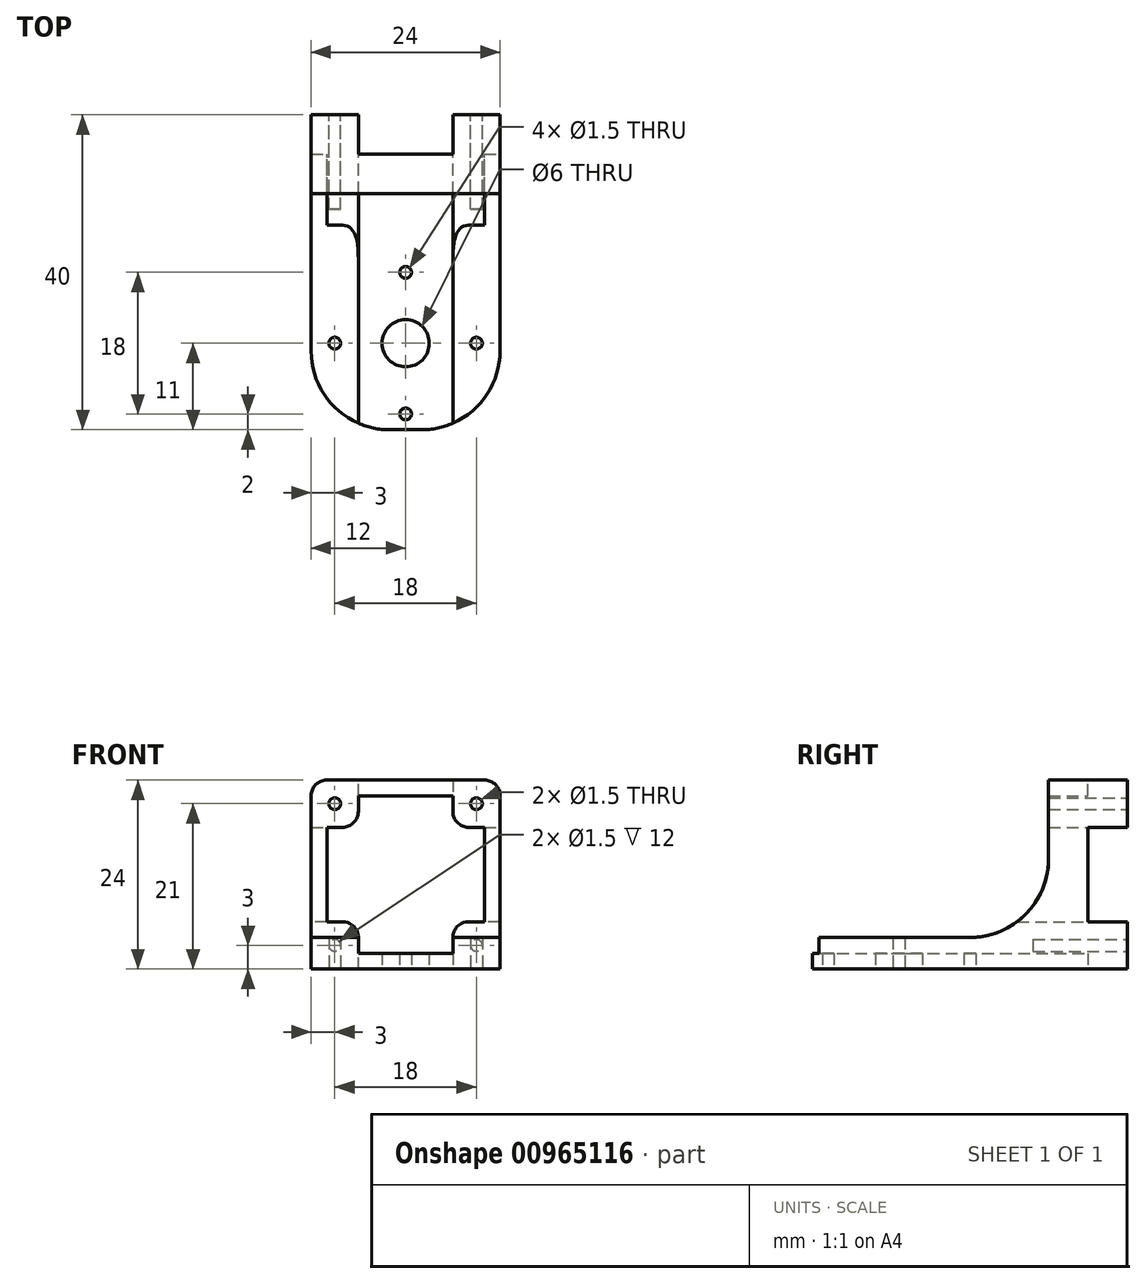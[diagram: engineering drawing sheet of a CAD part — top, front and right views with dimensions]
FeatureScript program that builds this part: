
annotation { "Feature Type Name" : "Feature", "Feature Type Description" : "" }
export const myFeature = defineFeature(function(context is Context, id is Id, definition is map)
    precondition{}
    {
        {
            var Q0;
            Q0=qCreatedBy(makeId("Top.planeOp"),FACE);
            var sketch = newSketch(context, id + "F0", { "sketchPlane" : qUnion([Q0])});
            skLineSegment(sketch, "E0.bottom", {"start": v(0, 0) * mm, "end": v(24, 0) * mm});
            skLineSegment(sketch, "E0.top", {"start": v(0, 35) * mm, "end": v(24, 35) * mm});
            skLineSegment(sketch, "E0.left", {"start": v(0, 0) * mm, "end": v(0, 35) * mm});
            skLineSegment(sketch, "E0.right", {"start": v(24, 0) * mm, "end": v(24, 35) * mm});
            skLineSegment(sketch, "E1", {"start": v(2.83, 11) * mm, "end": v(19.55, 11) * mm, "construction": true});
            skLineSegment(sketch, "E2", {"start": v(12, 2.3) * mm, "end": v(12, 16.8) * mm, "construction": true});
            skLineSegment(sketch, "E3", {"start": v(2, 21) * mm, "end": v(22, 1) * mm, "construction": true});
            skLineSegment(sketch, "E4", {"start": v(22, 21) * mm, "end": v(2, 1) * mm, "construction": true});
            skCircle(sketch, "E5", {"center": v(12, 2) * mm, "radius": 0.75 * mm});
            skCircle(sketch, "E6", {"center": v(3, 11) * mm, "radius": 0.75 * mm});
            skCircle(sketch, "E7", {"center": v(12, 20) * mm, "radius": 0.75 * mm});
            skCircle(sketch, "E8", {"center": v(21, 11) * mm, "radius": 0.75 * mm});
            skCircle(sketch, "E9", {"center": v(12, 11) * mm, "radius": 3 * mm});
            skSolve(sketch);
        }
        {
            var Q0;
            Q0=makeQuery(id+"F0.imprint","IMPRINT",FACE,{"disambiguationData":[TD([[makeQuery(id+"F0.imprint","IMPRINT",EDGE,{"derivedFrom":sQuery(id+"F0.wireOp",EDGE,"E0.bottom")}),1.0]])]});
            extrude(context, id + "F1", {"entities" : qUnion([Q0]), "depth" : 24 * mm, "offsetDistance" : 25 * mm});
        }
        {
            var Q0;
            Q0=makeQuery(id+"F1.opExtrude","SWEPT_FACE",FACE,{"disambiguationData":[OSD([sQuery(id+"F0.wireOp",EDGE,"E0.top")])]});
            var sketch = newSketch(context, id + "F2", { "sketchPlane" : qUnion([Q0])});
            skCircle(sketch, "E10", {"center": v(-3, 3) * mm, "radius": 0.75 * mm});
            skCircle(sketch, "E11", {"center": v(-21, 3) * mm, "radius": 0.75 * mm});
            skCircle(sketch, "E12", {"center": v(-21, 21) * mm, "radius": 0.75 * mm});
            skCircle(sketch, "E13", {"center": v(-3, 21) * mm, "radius": 0.75 * mm});
            skLineSegment(sketch, "E14", {"start": v(-6, 22) * mm, "end": v(-18, 22) * mm});
            skLineSegment(sketch, "E15", {"start": v(-22, 18) * mm, "end": v(-22, 6) * mm});
            skLineSegment(sketch, "E16", {"start": v(-18, 2) * mm, "end": v(-6, 2) * mm});
            skLineSegment(sketch, "E17", {"start": v(-2, 18) * mm, "end": v(-2, 6) * mm});
            skLineSegment(sketch, "E18", {"start": v(-18, 22) * mm, "end": v(-18, 18) * mm});
            skLineSegment(sketch, "E19", {"start": v(-18, 18) * mm, "end": v(-22, 18) * mm});
            skLineSegment(sketch, "E20", {"start": v(-22, 6) * mm, "end": v(-18, 6) * mm});
            skLineSegment(sketch, "E21", {"start": v(-18, 6) * mm, "end": v(-18, 2) * mm});
            skLineSegment(sketch, "E22", {"start": v(-6, 2) * mm, "end": v(-6, 6) * mm});
            skLineSegment(sketch, "E23", {"start": v(-6, 6) * mm, "end": v(-2, 6) * mm});
            skLineSegment(sketch, "E24", {"start": v(-2, 18) * mm, "end": v(-6, 18) * mm});
            skLineSegment(sketch, "E25", {"start": v(-6, 18) * mm, "end": v(-6, 22) * mm});
            skLineSegment(sketch, "E26.bottom", {"start": v(-18, 22) * mm, "end": v(-6, 22) * mm});
            skLineSegment(sketch, "E26.top", {"start": v(-18, 24) * mm, "end": v(-6, 24) * mm});
            skLineSegment(sketch, "E26.left", {"start": v(-18, 22) * mm, "end": v(-18, 24) * mm});
            skLineSegment(sketch, "E26.right", {"start": v(-6, 22) * mm, "end": v(-6, 24) * mm});
            skLineSegment(sketch, "E27.bottom", {"start": v(-2, 18) * mm, "end": v(0, 18) * mm});
            skLineSegment(sketch, "E27.top", {"start": v(-2, 6) * mm, "end": v(0, 6) * mm});
            skLineSegment(sketch, "E27.right", {"start": v(0, 18) * mm, "end": v(0, 6) * mm});
            skLineSegment(sketch, "E28.bottom", {"start": v(-22, 18) * mm, "end": v(-24, 18) * mm});
            skLineSegment(sketch, "E28.top", {"start": v(-22, 6) * mm, "end": v(-24, 6) * mm});
            skLineSegment(sketch, "E28.right", {"start": v(-24, 18) * mm, "end": v(-24, 6) * mm});
            skLineSegment(sketch, "E29.top", {"start": v(-18, 0) * mm, "end": v(-6, 0) * mm});
            skLineSegment(sketch, "E29.left", {"start": v(-18, 2) * mm, "end": v(-18, 0) * mm});
            skLineSegment(sketch, "E29.right", {"start": v(-6, 2) * mm, "end": v(-6, 0) * mm});
            skSolve(sketch);
        }
        {
            var Q0;
            Q0=makeQuery(id+"F2.imprint","IMPRINT",FACE,{"disambiguationData":[TD([[makeQuery(id+"F2.imprint","IMPRINT",EDGE,{"derivedFrom":sQuery(id+"F2.wireOp",EDGE,"E12")}),1.0]])]});
            var Q1;
            Q1=makeQuery(id+"F2.imprint","IMPRINT",FACE,{"disambiguationData":[TD([[makeQuery(id+"F2.imprint","IMPRINT",EDGE,{"derivedFrom":sQuery(id+"F2.wireOp",EDGE,"E13")}),1.0]])]});
            var Q2;
            Q2=makeQuery(id+"F2.imprint","IMPRINT",FACE,{"disambiguationData":[TD([[makeQuery(id+"F2.imprint","IMPRINT",EDGE,{"derivedFrom":sQuery(id+"F2.wireOp",EDGE,"E10")}),1.0]])]});
            var Q3;
            Q3=makeQuery(id+"F2.imprint","IMPRINT",FACE,{"disambiguationData":[TD([[makeQuery(id+"F2.imprint","IMPRINT",EDGE,{"derivedFrom":sQuery(id+"F2.wireOp",EDGE,"E11")}),1.0]])]});
            extrude(context, id + "F3", {"entities" : qUnion([Q0, Q1, Q2, Q3]), "operationType" : NewBodyOperationType.REMOVE, "oppositeDirection" : true, "depth" : 7 * mm, "offsetDistance" : 25 * mm});
        }
        {
            var Q0;
            Q0=makeQuery(id+"F2.imprint","IMPRINT",FACE,{"disambiguationData":[TD([[makeQuery(id+"F2.imprint","IMPRINT",EDGE,{"derivedFrom":sQuery(id+"F2.wireOp",EDGE,"E18")}),1.0]])]});
            extrude(context, id + "F4", {"entities" : qUnion([Q0]), "operationType" : NewBodyOperationType.REMOVE, "oppositeDirection" : true, "depth" : 100 * mm, "offsetDistance" : 25 * mm});
        }
        {
            var Q0;
            Q0=makeQuery(id+"F1.opExtrude","SWEPT_FACE",FACE,{"disambiguationData":[OSD([sQuery(id+"F0.wireOp",EDGE,"E0.left")])]});
            var sketch = newSketch(context, id + "F5", { "sketchPlane" : qUnion([Q0])});
            skLineSegment(sketch, "E30.bottom", {"start": v(0, 24) * mm, "end": v(-30, 24) * mm});
            skLineSegment(sketch, "E30.top", {"start": v(0, 4) * mm, "end": v(-30, 4) * mm});
            skLineSegment(sketch, "E30.left", {"start": v(0, 24) * mm, "end": v(0, 4) * mm});
            skLineSegment(sketch, "E30.right", {"start": v(-30, 24) * mm, "end": v(-30, 4) * mm});
            skSolve(sketch);
        }
        {
            var Q0;
            Q0=makeQuery(id+"F5.imprint","IMPRINT",FACE,{"disambiguationData":[TD([[makeQuery(id+"F5.imprint","IMPRINT",EDGE,{"derivedFrom":sQuery(id+"F5.wireOp",EDGE,"E30.bottom")}),1.0]])]});
            extrude(context, id + "F6", {"entities" : qUnion([Q0]), "operationType" : NewBodyOperationType.REMOVE, "oppositeDirection" : true, "depth" : 25 * mm, "offsetDistance" : 25 * mm});
        }
        {
            var Q0;
            Q0=makeQuery(id+"F2.imprint","IMPRINT",FACE,{"disambiguationData":[TD([[makeQuery(id+"F2.imprint","IMPRINT",EDGE,{"derivedFrom":sQuery(id+"F2.wireOp",EDGE,"E12")}),-1.0]])]});
            var Q1;
            Q1=makeQuery(id+"F2.imprint","IMPRINT",FACE,{"disambiguationData":[TD([[makeQuery(id+"F2.imprint","IMPRINT",EDGE,{"derivedFrom":sQuery(id+"F2.wireOp",EDGE,"E13")}),-1.0]])]});
            var Q2;
            Q2=makeQuery(id+"F2.imprint","IMPRINT",FACE,{"disambiguationData":[TD([[makeQuery(id+"F2.imprint","IMPRINT",EDGE,{"derivedFrom":sQuery(id+"F2.wireOp",EDGE,"E10")}),-1.0]])]});
            var Q3;
            Q3=makeQuery(id+"F2.imprint","IMPRINT",FACE,{"disambiguationData":[TD([[makeQuery(id+"F2.imprint","IMPRINT",EDGE,{"derivedFrom":sQuery(id+"F2.wireOp",EDGE,"E11")}),-1.0]])]});
            extrude(context, id + "F7", {"entities" : qUnion([Q0, Q1, Q2, Q3]), "operationType" : NewBodyOperationType.ADD, "depth" : 5 * mm, "offsetDistance" : 25 * mm});
        }
        {
            var Q0;
            Q0=makeQuery(id+"F4.boolean.opBoolean","COPY",EDGE,{"derivedFrom":makeQuery(id+"F4.opExtrude","SWEPT_EDGE",EDGE,{"disambiguationData":[OSD([sQuery(id+"F2.wireOp",EDGE,"E20"),sQuery(id+"F2.wireOp",EDGE,"E21")])]})});
            var Q1;
            {var subQ0=sQuery(id+"F2.wireOp",EDGE,"E25");var subQ1=sQuery(id+"F2.wireOp",EDGE,"E24");Q1=makeQuery(id+"F4.boolean.opBoolean","COPY",EDGE,{"disambiguationData":[TD([makeQuery(id+"F1.opExtrude","SWEPT_FACE",FACE,{"disambiguationData":[OSD([sQuery(id+"F0.wireOp",EDGE,"E0.top")])]}),makeQuery(id+"F1.opExtrude","SWEPT_FACE",FACE,{"disambiguationData":[OSD([sQuery(id+"F0.wireOp",EDGE,"zczxjooS-rRjf-LuSm-cy0b-x2i11LA2eNHv")])]}),makeQuery(id+"F4.opExtrude","SWEPT_FACE",FACE,{"disambiguationData":[OSD([subQ1])]}),makeQuery(id+"F4.opExtrude","SWEPT_FACE",FACE,{"disambiguationData":[OSD([subQ0])]})])],"derivedFrom":makeQuery(id+"F4.opExtrude","SWEPT_EDGE",EDGE,{"disambiguationData":[OSD([subQ1,subQ0])]})});}
            var Q2;
            Q2=makeQuery(id+"F4.boolean.opBoolean","COPY",EDGE,{"derivedFrom":makeQuery(id+"F4.opExtrude","SWEPT_EDGE",EDGE,{"disambiguationData":[OSD([sQuery(id+"F2.wireOp",EDGE,"E18"),sQuery(id+"F2.wireOp",EDGE,"E19")])]})});
            var Q3;
            Q3=makeQuery(id+"F1.opExtrude","CAP_EDGE",EDGE,{"disambiguationData":[OSD([sQuery(id+"F0.wireOp",EDGE,"E0.left")])],"isStart":false});
            var Q4;
            Q4=makeQuery(id+"F1.opExtrude","CAP_EDGE",EDGE,{"disambiguationData":[OSD([sQuery(id+"F0.wireOp",EDGE,"E0.right")])],"isStart":false});
            var Q5;
            {var subQ0=sQuery(id+"F2.wireOp",EDGE,"E22");var subQ1=sQuery(id+"F2.wireOp",EDGE,"E23");Q5=makeQuery(id+"F4.boolean.opBoolean","COPY",EDGE,{"disambiguationData":[TD([makeQuery(id+"F1.opExtrude","SWEPT_FACE",FACE,{"disambiguationData":[OSD([sQuery(id+"F0.wireOp",EDGE,"E0.top")])]}),makeQuery(id+"F1.opExtrude","SWEPT_FACE",FACE,{"disambiguationData":[OSD([sQuery(id+"F0.wireOp",EDGE,"zczxjooS-rRjf-LuSm-cy0b-x2i11LA2eNHv")])]}),makeQuery(id+"F4.opExtrude","SWEPT_FACE",FACE,{"disambiguationData":[OSD([subQ0])]}),makeQuery(id+"F4.opExtrude","SWEPT_FACE",FACE,{"disambiguationData":[OSD([subQ1])]})])],"derivedFrom":makeQuery(id+"F4.opExtrude","SWEPT_EDGE",EDGE,{"disambiguationData":[OSD([subQ0,subQ1])]})});}
            fillet(context, id + "F8", {"entities" : qUnion([Q0, Q1, Q2, Q3, Q4, Q5]), "tangentPropagation" : true, "radius" : 2 * mm, "defaultsChanged" : true, "vertexSettings" : [], "allowEdgeOverflow" : false});
        }
        {
            var Q0;
            {var subQ0=sQuery(id+"F5.wireOp",EDGE,"E30.top");var subQ1=sQuery(id+"F5.wireOp",EDGE,"E30.right");Q0=makeQuery(id+"F6.boolean.opBoolean","COPY",EDGE,{"disambiguationData":[TD([makeQuery(id+"F1.opExtrude","SWEPT_FACE",FACE,{"disambiguationData":[OSD([sQuery(id+"F0.wireOp",EDGE,"E0.right")])]})])],"derivedFrom":makeQuery(id+"F6.opExtrude","SWEPT_EDGE",EDGE,{"disambiguationData":[OSD([subQ0,subQ1])]})});}
            var Q1;
            {var subQ0=sQuery(id+"F5.wireOp",EDGE,"E30.right");var subQ1=sQuery(id+"F5.wireOp",EDGE,"E30.top");Q1=makeQuery(id+"F6.boolean.opBoolean","COPY",EDGE,{"disambiguationData":[TD([makeQuery(id+"F1.opExtrude","SWEPT_FACE",FACE,{"disambiguationData":[OSD([sQuery(id+"F0.wireOp",EDGE,"E0.left")])]})])],"derivedFrom":makeQuery(id+"F6.opExtrude","SWEPT_EDGE",EDGE,{"disambiguationData":[OSD([subQ1,subQ0])]})});}
            var Q2;
            Q2=makeQuery(id+"F1.opExtrude","SWEPT_EDGE",EDGE,{"disambiguationData":[OSD([sQuery(id+"F0.wireOp",EDGE,"E0.bottom"),sQuery(id+"F0.wireOp",EDGE,"E0.right")])]});
            var Q3;
            Q3=makeQuery(id+"F1.opExtrude","SWEPT_EDGE",EDGE,{"disambiguationData":[OSD([sQuery(id+"F0.wireOp",EDGE,"E0.bottom"),sQuery(id+"F0.wireOp",EDGE,"E0.left")])]});
            fillet(context, id + "F9", {"entities" : qUnion([Q0, Q1, Q2, Q3]), "tangentPropagation" : true, "radius" : 10 * mm, "defaultsChanged" : true, "vertexSettings" : [], "allowEdgeOverflow" : false});
        }
    });
